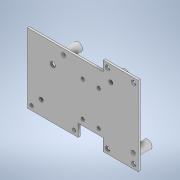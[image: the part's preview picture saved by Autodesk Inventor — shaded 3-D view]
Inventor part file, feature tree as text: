
AUTODESK INVENTOR PART (.ipt)
format: ipt  version: 2021 (Build 250183000, 183)  size: 645,120 bytes
history: native  units: mm
features: reference x24, other x9, sketch x6, extrude x3, plane x2, chamfer x2
ambient origin geometry x8: Origin, YZ Plane, XZ Plane, XY Plane, X Axis, Y Axis, Z Axis, Center Point
bodies: Volumenkörper1 (feature_tree)
feature tree (46):
  plane  "Arbeitsebene1"
  extrude  "Extrusion1"  Depth=1.0mm
  extrude  "Extrusion2"  Depth=1.0mm
  plane  "Arbeitsebene2"
  chamfer  "Fase1"  Distance=1.0mm
  sketch  "Skizze6"  dims[d6=1.0mm]
  other  "Spirale1"
  sketch  "Skizzenbasierte Anordnung1"  dims[d0=1.0mm d1=1.0mm]
  chamfer  "Fase2"  Distance=1.0mm
  extrude  "Extrusion3"  Depth=1.6mm TaperAngle=0.0deg
  sketch  "Skizze1"  dims[d2=1.0mm d3=1.0mm]
  reference  "Referenz1"
  reference  "Referenz2"
  reference  "Referenz3"
  reference  "Referenz4"
  reference  "Referenz5"
  reference  "Referenz6"
  reference  "Referenz7"
  reference  "Referenz8"
  reference  "Referenz9"
  reference  "Referenz10"
  reference  "Referenz11"
  reference  "Referenz12"
  reference  "Referenz13"
  reference  "Referenz14"
  reference  "Referenz15"
  reference  "Referenz16"
  reference  "Referenz17"
  reference  "Referenz18"
  reference  "Referenz19"
  reference  "Referenz20"
  reference  "Referenz21"
  reference  "Referenz22"
  reference  "Referenz23"
  reference  "Referenz24"
  sketch  "Skizze2"  dims[d4=1.0mm]
  other  "Arbeitsachse1"
  sketch  "Skizze5"  dims[d5=1.0mm]
  sketch  "Skizze7"  dims[d7=2.0mm d8=1.0mm d9=1.0mm d10=1.6mm d11=0.0mm d16=10.0mm d17=0.0mm d18=2.0mm d19=0.2mm d20=0.2mm d21=0.2mm d22=2.0mm d23=2.0mm d24=2.0mm d25=2.0mm d26=2.0mm d27=0.2mm d28=0.2mm d29=3.1505mm d30=1.92mm d31=1.92mm d32=1.92mm d33=1.92mm d34=60.0deg d35=3.8mm d36=0.6mm d37=3.1505mm d38=0.32475mm d39=0.06495mm d40=60.0deg d41=3.8mm d42=0.6mm d43=3.1505mm d44=0.5196mm d45=0.6mm d46=10.0mm d47=10.0mm d48=0.0mm d49=90.0deg d50=90.0deg d51=0.0mm d52=0.0mm d53=0.5mm d54=2.0mm d55=45.0deg d56=1.0mm d57=1.0mm d58=1.0mm d59=1.0mm d60=1.0mm d61=1.0mm d62=1.0mm d63=1.0mm d64=1.0mm d65=1.0mm d66=1.0mm d67=2.0mm d68=0.0mm d69=0.4mm d70=2.0mm d71=45.0deg]
  other  "<userpath>\Desktop\Bachelorarbeit\CAD\00_RobotAssembly.iam"
  other  "00_RobotAssembly.iam"
  other  "01_CaseBottom:1"
  other  "dc-dc-5a-cc:1"
  other  "PCB^dc-dc-5a-cc_1"
  other  "PCB_PowerSupply:1"
  other  "Step_Down_USB:1"
